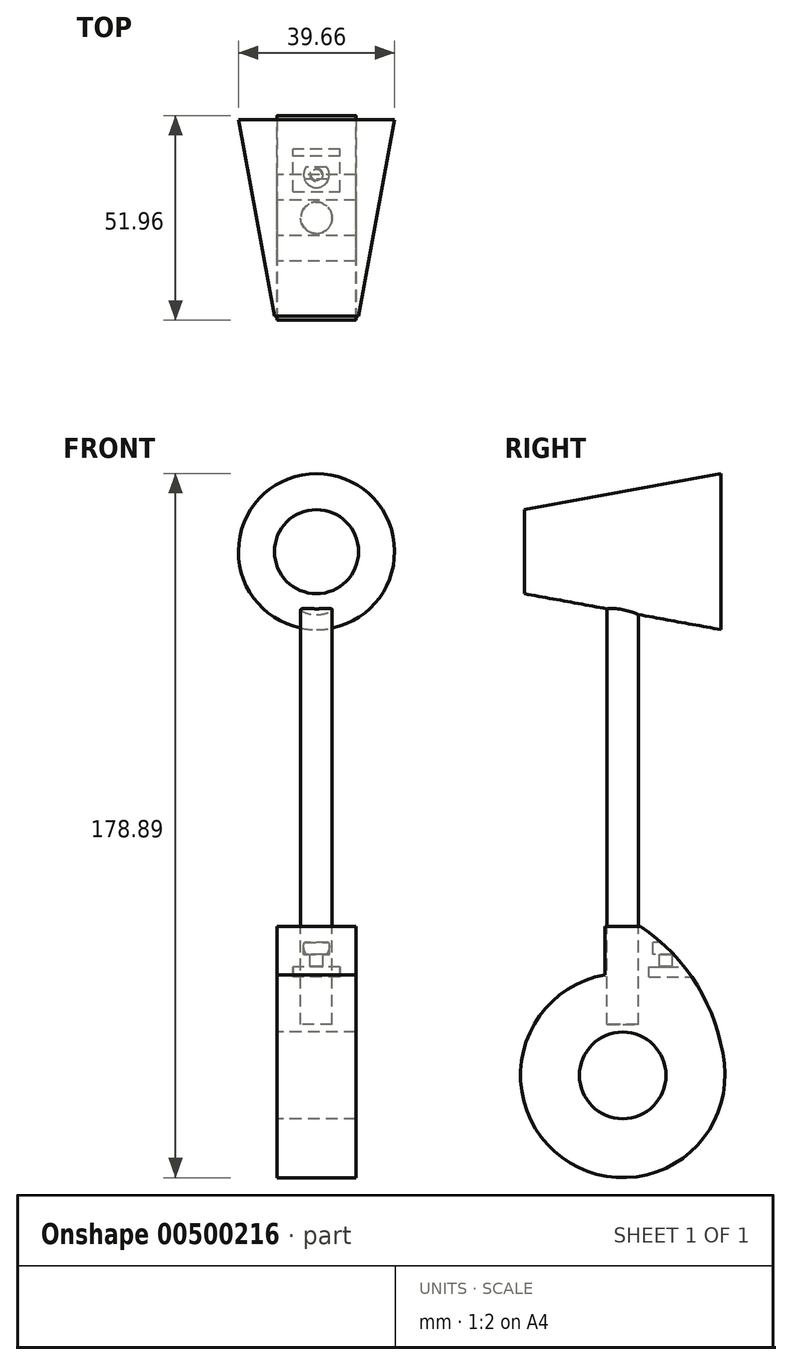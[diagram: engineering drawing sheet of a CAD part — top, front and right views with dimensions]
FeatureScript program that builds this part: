
annotation { "Feature Type Name" : "Feature", "Feature Type Description" : "" }
export const myFeature = defineFeature(function(context is Context, id is Id, definition is map)
    precondition{}
    {
        {
            var Q0;
            Q0=qCreatedBy(makeId("Right.planeOp"),FACE);
            var sketch = newSketch(context, id + "F0", { "sketchPlane" : qUnion([Q0])});
            skCircle(sketch, "E0", {"center": v(0, 31.77) * mm, "radius": 11 * mm});
            skCircle(sketch, "E1", {"center": v(0, 31.77) * mm, "radius": 4 * mm});
            skCircle(sketch, "E2", {"center": v(0, 31.77) * mm, "radius": 25.98 * mm});
            skLineSegment(sketch, "E3.bottom", {"start": v(4.5, 45.82) * mm, "end": v(-4.5, 45.82) * mm});
            skLineSegment(sketch, "E3.top", {"start": v(4.5, 69.68) * mm, "end": v(-4.5, 69.68) * mm});
            skLineSegment(sketch, "E3.left", {"start": v(4.5, 45.82) * mm, "end": v(4.5, 69.68) * mm});
            skLineSegment(sketch, "E3.right", {"start": v(-4.5, 45.82) * mm, "end": v(-4.5, 69.68) * mm});
            skPoint(sketch, "E3.middle", {"position": v(0, 57.75) * mm});
            skArc(sketch, "E4", {"start": v(25.8, 34.85) * mm, "mid": v(18.95, 54.59) * mm, "end": v(4.5, 69.68) * mm});
            skArc(sketch, "E5.MirrorCS", {"start": v(-25.8, 34.85) * mm, "mid": v(-18.95, 54.59) * mm, "end": v(-4.5, 69.68) * mm});
            skSolve(sketch);
        }
        {
            var Q0;
            Q0=makeQuery(id+"F0.imprint","IMPRINT",FACE,{"disambiguationData":[TD([[makeQuery(id+"F0.imprint","IMPRINT",EDGE,{"derivedFrom":sQuery(id+"F0.wireOp",EDGE,"E0")}),-1.0]])]});
            var Q1;
            {var subQ0=sQuery(id+"F0.wireOp",EDGE,"E4");Q1=makeQuery(id+"F0.imprint","IMPRINT",FACE,{"disambiguationData":[TD([[makeQuery(id+"F0.imprint","IMPRINT",EDGE,{"derivedFrom":subQ0}),1.0]])]});}
            var Q2;
            {var subQ0=sQuery(id+"F0.wireOp",EDGE,"E5.MirrorCS");Q2=makeQuery(id+"F0.imprint","IMPRINT",FACE,{"disambiguationData":[TD([[makeQuery(id+"F0.imprint","IMPRINT",EDGE,{"derivedFrom":subQ0}),-1.0]])]});}
            var Q3;
            {var subQ5=sQuery(id+"F0.wireOp",EDGE,"E3.bottom");Q3=makeQuery(id+"F0.imprint","IMPRINT",FACE,{"disambiguationData":[TD([[makeQuery(id+"F0.imprint","IMPRINT",EDGE,{"derivedFrom":subQ5}),-1.0]])]});}
            var Q4;
            {var subQ5=sQuery(id+"F0.wireOp",EDGE,"E3.top");Q4=makeQuery(id+"F0.imprint","IMPRINT",FACE,{"disambiguationData":[TD([[makeQuery(id+"F0.imprint","IMPRINT",EDGE,{"derivedFrom":subQ5}),1.0]])]});}
            extrude(context, id + "F1", {"entities" : qUnion([Q0, Q1, Q2, Q3, Q4]), "depth" : 10 * mm, "hasSecondDirection" : true, "secondDirectionOppositeDirection" : true, "secondDirectionDepth" : 10 * mm});
        }
        {
            var Q0;
            Q0=makeQuery(id+"F1.opExtrude","SWEPT_FACE",FACE,{"disambiguationData":[OSD([sQuery(id+"F0.wireOp",EDGE,"E3.top")])]});
            var sketch = newSketch(context, id + "F2", { "sketchPlane" : qUnion([Q0])});
            skCircle(sketch, "E6", {"center": v(0, 0) * mm, "radius": 4 * mm});
            skSolve(sketch);
        }
        {
            var Q0;
            {var subQ0=sQuery(id+"F2.wireOp",EDGE,"E6");var subQ1=sQuery(id+"F0.wireOp",EDGE,"E3.top");var subQ2=makeQuery(id+"F1.opExtrude","SWEPT_EDGE",EDGE,{"disambiguationData":[OSD([subQ1,sQuery(id+"F0.wireOp",EDGE,"E3.left"),sQuery(id+"F0.wireOp",EDGE,"E4")])]});var subQ3=makeQuery(id+"F2.imprint","INTERSECT",VERTEX,{"disambiguationData":[OD(0.0)],"derivedFrom":[subQ2,subQ0]});Q0=makeQuery(id+"F2.imprint","IMPRINT",FACE,{"disambiguationData":[TD([[makeQuery(id+"F2.imprint","IMPRINT",EDGE,{"disambiguationData":[TD([[subQ3,-1.0]])],"derivedFrom":subQ0}),1.0]])]});}
            var Q1;
            {var subQ0=sQuery(id+"F2.wireOp",EDGE,"E6");var subQ1=makeQuery(id+"F1.opExtrude","SWEPT_EDGE",EDGE,{"disambiguationData":[OSD([sQuery(id+"F0.wireOp",EDGE,"E3.top"),sQuery(id+"F0.wireOp",EDGE,"E3.left"),sQuery(id+"F0.wireOp",EDGE,"E4")])]});var subQ2=makeQuery(id+"F2.imprint","INTERSECT",VERTEX,{"disambiguationData":[OD(0.0)],"derivedFrom":[subQ1,subQ0]});Q1=makeQuery(id+"F2.imprint","IMPRINT",FACE,{"disambiguationData":[TD([[makeQuery(id+"F2.imprint","IMPRINT",EDGE,{"disambiguationData":[TD([[subQ2,1.0]])],"derivedFrom":subQ0}),1.0]])]});}
            var Q2;
            {var subQ0=sQuery(id+"F2.wireOp",EDGE,"E6");var subQ1=makeQuery(id+"F1.opExtrude","SWEPT_EDGE",EDGE,{"disambiguationData":[OSD([sQuery(id+"F0.wireOp",EDGE,"E3.top"),sQuery(id+"F0.wireOp",EDGE,"E3.right"),sQuery(id+"F0.wireOp",EDGE,"E5.MirrorCS")])]});var subQ2=makeQuery(id+"F2.imprint","INTERSECT",VERTEX,{"disambiguationData":[OD(0.0)],"derivedFrom":[subQ1,subQ0]});Q2=makeQuery(id+"F2.imprint","IMPRINT",FACE,{"disambiguationData":[TD([[makeQuery(id+"F2.imprint","IMPRINT",EDGE,{"disambiguationData":[TD([[subQ2,-1.0]])],"derivedFrom":subQ0}),1.0]])]});}
            extrude(context, id + "F3", {"entities" : qUnion([Q0, Q1, Q2]), "operationType" : NewBodyOperationType.REMOVE, "oppositeDirection" : true, "depth" : 25 * mm});
        }
        {
            var Q0;
            Q0=qCreatedBy(makeId("Front.planeOp"),FACE);
            cPlane(context, id + "F4", {"entities" : qUnion([Q0]), "cplaneType" : CPlaneType.OFFSET, "offset" : 25 * mm, "oppositeDirection" : true, "width" : 150 * mm, "height" : 150 * mm});
        }
        {
            var Q0;
            Q0=qCreatedBy(id+"F4.planeOp",FACE);
            var sketch = newSketch(context, id + "F5", { "sketchPlane" : qUnion([Q0])});
            skLineSegment(sketch, "E7.bottom", {"start": v(-6, 56.85) * mm, "end": v(6, 56.85) * mm});
            skLineSegment(sketch, "E7.top", {"start": v(-6, 59.35) * mm, "end": v(6, 59.35) * mm});
            skLineSegment(sketch, "E7.left", {"start": v(-6, 56.85) * mm, "end": v(-6, 59.35) * mm});
            skLineSegment(sketch, "E7.right", {"start": v(6, 56.85) * mm, "end": v(6, 59.35) * mm});
            skPoint(sketch, "E7.middle", {"position": v(0, 58.1) * mm});
            skSolve(sketch);
        }
        {
            var Q0;
            Q0=makeQuery(id+"F5.imprint","IMPRINT",FACE,{"disambiguationData":[TD([[makeQuery(id+"F5.imprint","IMPRINT",EDGE,{"derivedFrom":sQuery(id+"F5.wireOp",EDGE,"E7.bottom")}),1.0]])]});
            extrude(context, id + "F6", {"entities" : qUnion([Q0]), "operationType" : NewBodyOperationType.REMOVE, "depth" : 18.4 * mm});
        }
        {
            var Q0;
            Q0=qCreatedBy(makeId("Top.planeOp"),FACE);
            cPlane(context, id + "F7", {"entities" : qUnion([Q0]), "cplaneType" : CPlaneType.OFFSET, "offset" : 65.5 * mm, "width" : 150 * mm, "height" : 150 * mm});
        }
        {
            var Q0;
            Q0=qCreatedBy(id+"F7.planeOp",FACE);
            var sketch = newSketch(context, id + "F8", { "sketchPlane" : qUnion([Q0])});
            skCircle(sketch, "E8", {"center": v(0, 10.92) * mm, "radius": 1.5 * mm});
            skSolve(sketch);
        }
        {
            var Q0;
            Q0=sQuery(id+"F8.wireOp",VERTEX,"E8.center");
            var Q1;
            Q1=makeQuery(id+"F1.opExtrude","SWEPT_BODY",BODY,{"disambiguationData":[OSD([sQuery(id+"F0.wireOp",EDGE,"E0"),sQuery(id+"F0.wireOp",EDGE,"E2"),sQuery(id+"F0.wireOp",EDGE,"E3.top"),sQuery(id+"F0.wireOp",EDGE,"E4"),sQuery(id+"F0.wireOp",EDGE,"E5.MirrorCS")])]});
            hole(context, id + "F9", {"style" : HoleStyle.C_BORE, "endStyle" : HoleEndStyle.BLIND, "standardTappedOrClearance" : lookupTablePath({ "standard" : "ISO", "fit" : "Normal", "size" : "M3", "type" : "Clearance" }), "standardBlindInLast" : lookupTablePath({ "fit" : "Standard", "standard" : "ISO", "size" : "M3", "type" : "Clearance" }), "holeDiameter" : 3.3 * mm, "cBoreDiameter" : 6.5 * mm, "cBoreDepth" : 3 * mm, "holeDepth" : 6 * mm, "isTappedThrough" : true, "tappedDepth" : 12 * mm, "tapClearance" : 3, "locations" : qUnion([Q0]), "scope" : qUnion([Q1])});
        }
        {
            var Q0;
            Q0 = qSketchRegion(id + "F2", true);
            extrude(context, id + "F10", {"entities" : qUnion([Q0]), "depth" : 100 * mm});
        }
        {
            var Q0;
            Q0=qCreatedBy(id+"F4.planeOp",FACE);
            var sketch = newSketch(context, id + "F11", { "sketchPlane" : qUnion([Q0])});
            skCircle(sketch, "E9", {"center": v(0, 164.85) * mm, "radius": 19.83 * mm});
            skSolve(sketch);
        }
        {
            var Q0;
            Q0=qCreatedBy(makeId("Front.planeOp"),FACE);
            cPlane(context, id + "F12", {"entities" : qUnion([Q0]), "cplaneType" : CPlaneType.OFFSET, "offset" : 25 * mm, "width" : 150 * mm, "height" : 150 * mm});
        }
        {
            var Q0;
            Q0=qCreatedBy(id+"F12.planeOp",FACE);
            var sketch = newSketch(context, id + "F13", { "sketchPlane" : qUnion([Q0])});
            skCircle(sketch, "E10", {"center": v(0, 164.85) * mm, "radius": 10.68 * mm});
            skSolve(sketch);
        }
        {
            var Q1;
            Q1=makeQuery(id+"F13.imprint","IMPRINT",FACE,{"disambiguationData":[TD([[makeQuery(id+"F13.imprint","IMPRINT",EDGE,{"derivedFrom":sQuery(id+"F13.wireOp",EDGE,"E10")}),1.0]])]});
            var Q2;
            Q2=makeQuery(id+"F11.imprint","IMPRINT",FACE,{"disambiguationData":[TD([[makeQuery(id+"F11.imprint","IMPRINT",EDGE,{"derivedFrom":sQuery(id+"F11.wireOp",EDGE,"E9")}),1.0]])]});
            loft(context, id + "F14", {"operationType" : NewBodyOperationType.ADD, "sheetProfilesArray" : [{ "sheetProfileEntities" : qUnion([Q1]) }, { "sheetProfileEntities" : qUnion([Q2]) }]});
        }
        {
            var Q0;
            Q0=makeQuery(id+"F11.imprint","IMPRINT",FACE,{"disambiguationData":[TD([[makeQuery(id+"F11.imprint","IMPRINT",EDGE,{"derivedFrom":sQuery(id+"F11.wireOp",EDGE,"E9")}),1.0]])]});
            var sketch = newSketch(context, id + "F15", { "sketchPlane" : qUnion([Q0])});
            skArc(sketch, "E11", {"start": v(0, 145.02) * mm, "mid": v(19.83, 164.85) * mm, "end": v(0, 184.68) * mm});
            skLineSegment(sketch, "E12", {"start": v(0, 184.68) * mm, "end": v(0, 58.43) * mm, "construction": true});
            skSolve(sketch);
        }
        {
            var Q0;
            Q0 = qConstructionFilter(qBodyType(qCreatedBy(id + "F15" ,EDGE), BodyType.WIRE), ConstructionObject.NO);
            var Q1;
            Q1=sQuery(id+"F15.wireOp",EDGE,"E12");
            revolve(context, id + "F16", {"bodyType" : ToolBodyType.SURFACE, "surfaceEntities" : qUnion([Q0]), "axis" : qUnion([Q1]), "revolveType" : RevolveType.FULL});
        }
    });
